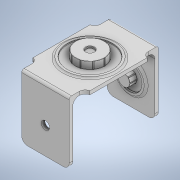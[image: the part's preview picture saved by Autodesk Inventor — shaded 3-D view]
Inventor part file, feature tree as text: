
AUTODESK INVENTOR PART (.ipt)
format: ipt  version: 2022 (Build 260153000, 153)  size: 580,608 bytes
history: native  units: mm
features: extrude x11, fillet x11, sketch x11, other x4, pattern_circular x2, projected_geometry x2, mirror x1
ambient origin geometry x8: Origin, YZ Plane, XZ Plane, XY Plane, X Axis, Y Axis, Z Axis, Center Point
bodies: Body1 (feature_tree)
feature tree (42):
  other  "Твердое тело1"
  extrude  "Выдавливание1"  Depth=40.0mm
  extrude  "Выдавливание2"  Depth=75.0mm
  extrude  "Выдавливание3"  Depth=3.0mm TaperAngle=0.0deg
  extrude  "Выдавливание5"  Depth=37.8mm
  fillet  "Сопряжение1"  Radius=2.0mm
  fillet  "Сопряжение3"  Radius=1.0mm
  other  "РабПлоскость1"
  extrude  "Выдавливание6"  Depth=24.2mm
  fillet  "Сопряжение4"  Radius=6.0mm
  fillet  "Сопряжение5"  Radius=48.0mm
  mirror  "Зеркальное отражение2"
  extrude  "Выдавливание7"  Depth=25.0mm
  extrude  "Выдавливание8"  Depth=3.0mm TaperAngle=0.0deg
  extrude  "Выдавливание9"  Depth=2.0mm
  fillet  "Сопряжение6"  Radius=5.0mm
  extrude  "Выдавливание10"  Depth=50.0mm
  fillet  "Сопряжение7"  Radius=3.0mm
  other  "РабОсь1"
  pattern_circular  "Круговой массив1"  [2 undecoded]
  fillet  "Сопряжение8"  Radius=5.0mm
  extrude  "Выдавливание11"  Depth=40.0mm
  fillet  "Сопряжение9"  Radius=7.0mm
  other  "РабОсь2"
  pattern_circular  "Круговой массив2"  [2 undecoded]
  fillet  "Сопряжение10"  Radius=21.0mm
  fillet  "Сопряжение11"  Radius=2.0mm
  extrude  "Выдавливание12"  Depth=1.4mm TaperAngle=0.0deg
  fillet  "Сопряжение12"  Radius=10.0mm
  sketch  "Эскиз1"
  sketch  "Эскиз2"
  sketch  "Эскиз3"
  sketch  "Эскиз5"
  sketch  "Эскиз6"
  sketch  "Эскиз7"
  projected_geometry  "Спроецированная петля1"
  sketch  "Эскиз8"
  sketch  "Эскиз9"
  sketch  "Эскиз10"
  sketch  "Эскиз11"
  projected_geometry  "Спроецированная петля2"
  sketch  "Эскиз15"
note: 4 required parameter values undecoded (feature->parameter linkage not recoverable at this tier; creation-order binding heuristic only, values carry confidence <= 0.55)
